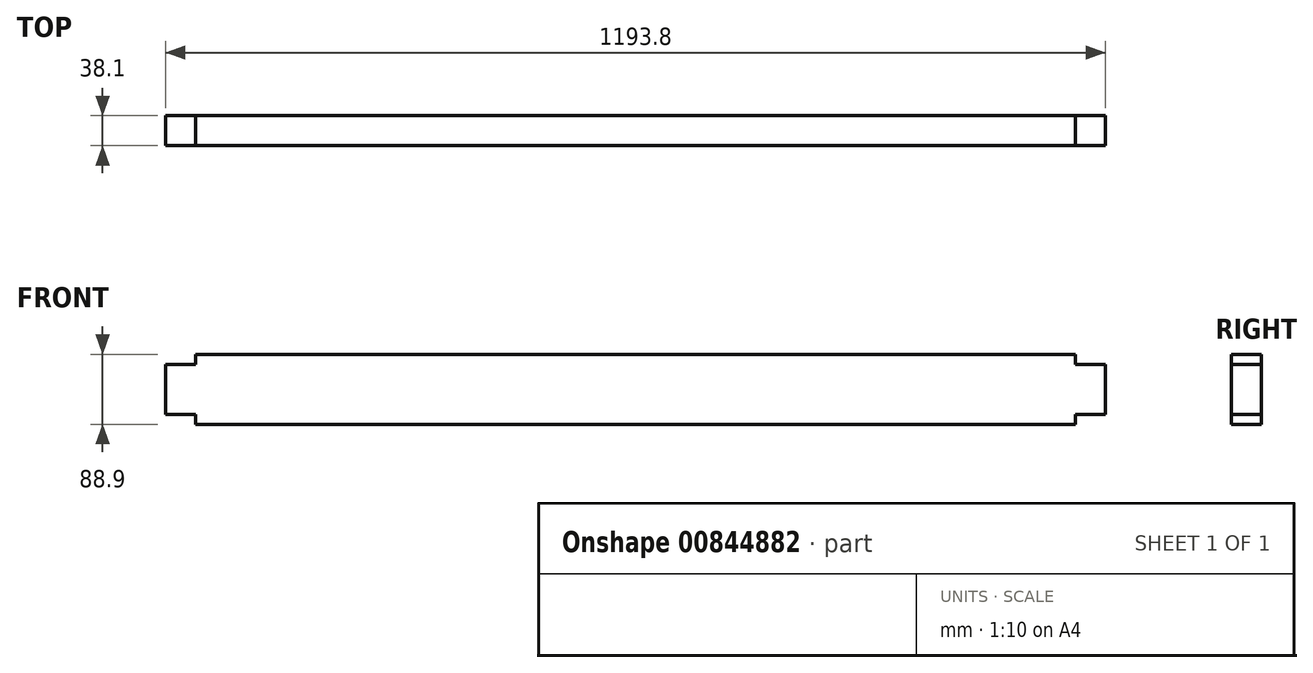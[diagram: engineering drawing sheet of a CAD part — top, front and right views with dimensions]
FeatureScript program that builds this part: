
annotation { "Feature Type Name" : "Feature", "Feature Type Description" : "" }
export const myFeature = defineFeature(function(context is Context, id is Id, definition is map)
    precondition{}
    {
        {
            var Q0;
            Q0=qCreatedBy(makeId("Right.planeOp"),FACE);
            var sketch = newSketch(context, id + "F0", { "sketchPlane" : qUnion([Q0])});
            skLineSegment(sketch, "E0.bottom", {"start": v(0, 0) * mm, "end": v(38.1, 0) * mm});
            skLineSegment(sketch, "E0.top", {"start": v(0, 88.9) * mm, "end": v(38.1, 88.9) * mm});
            skLineSegment(sketch, "E0.left", {"start": v(0, 0) * mm, "end": v(0, 88.9) * mm});
            skLineSegment(sketch, "E0.right", {"start": v(38.1, 0) * mm, "end": v(38.1, 88.9) * mm});
            skSolve(sketch);
        }
        {
            var Q0;
            Q0=makeQuery(id+"F0.imprint","IMPRINT",FACE,{"disambiguationData":[TD([[makeQuery(id+"F0.imprint","IMPRINT",EDGE,{"derivedFrom":sQuery(id+"F0.wireOp",EDGE,"E0.bottom")}),1.0]])]});
            extrude(context, id + "F1", {"entities" : qUnion([Q0]), "oppositeDirection" : true, "depth" : 1117.6 * mm, "offsetDistance" : 25.4 * mm});
        }
        {
            var Q0;
            Q0=makeQuery(id+"F1.opExtrude","CAP_FACE",FACE,{"disambiguationData":[OSD([sQuery(id+"F0.wireOp",EDGE,"E0.bottom"),sQuery(id+"F0.wireOp",EDGE,"E0.top"),sQuery(id+"F0.wireOp",EDGE,"E0.left"),sQuery(id+"F0.wireOp",EDGE,"E0.right")])],"isStart":true});
            var sketch = newSketch(context, id + "F2", { "sketchPlane" : qUnion([Q0])});
            skLineSegment(sketch, "E1.bottom", {"start": v(0, 76.2) * mm, "end": v(38.1, 76.2) * mm});
            skLineSegment(sketch, "E1.top", {"start": v(0, 12.7) * mm, "end": v(38.1, 12.7) * mm});
            skLineSegment(sketch, "E1.left", {"start": v(0, 76.2) * mm, "end": v(0, 12.7) * mm});
            skLineSegment(sketch, "E1.right", {"start": v(38.1, 76.2) * mm, "end": v(38.1, 12.7) * mm});
            skSolve(sketch);
        }
        {
            var Q0;
            Q0=makeQuery(id+"F2.imprint","IMPRINT",FACE,{"disambiguationData":[TD([[makeQuery(id+"F2.imprint","IMPRINT",EDGE,{"derivedFrom":sQuery(id+"F2.wireOp",EDGE,"E1.bottom")}),-1.0]])]});
            extrude(context, id + "F3", {"entities" : qUnion([Q0]), "operationType" : NewBodyOperationType.ADD, "depth" : 38.1 * mm, "offsetDistance" : 25.4 * mm});
        }
        {
            var Q0;
            Q0=makeQuery(id+"F1.opExtrude","CAP_FACE",FACE,{"disambiguationData":[OSD([sQuery(id+"F0.wireOp",EDGE,"E0.bottom"),sQuery(id+"F0.wireOp",EDGE,"E0.top"),sQuery(id+"F0.wireOp",EDGE,"E0.left"),sQuery(id+"F0.wireOp",EDGE,"E0.right")])],"isStart":false});
            var sketch = newSketch(context, id + "F4", { "sketchPlane" : qUnion([Q0])});
            skLineSegment(sketch, "E2.bottom", {"start": v(-38.1, 76.2) * mm, "end": v(0, 76.2) * mm});
            skLineSegment(sketch, "E2.top", {"start": v(-38.1, 12.7) * mm, "end": v(0, 12.7) * mm});
            skLineSegment(sketch, "E2.left", {"start": v(-38.1, 76.2) * mm, "end": v(-38.1, 12.7) * mm});
            skLineSegment(sketch, "E2.right", {"start": v(0, 76.2) * mm, "end": v(0, 12.7) * mm});
            skSolve(sketch);
        }
        {
            var Q0;
            Q0=makeQuery(id+"F4.imprint","IMPRINT",FACE,{"disambiguationData":[TD([[makeQuery(id+"F4.imprint","IMPRINT",EDGE,{"derivedFrom":sQuery(id+"F4.wireOp",EDGE,"E2.bottom")}),-1.0]])]});
            extrude(context, id + "F5", {"entities" : qUnion([Q0]), "operationType" : NewBodyOperationType.ADD, "depth" : 38.1 * mm, "offsetDistance" : 25.4 * mm});
        }
    });
